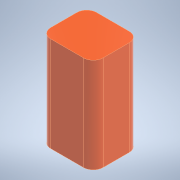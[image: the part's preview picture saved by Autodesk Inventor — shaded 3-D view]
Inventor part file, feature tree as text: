
AUTODESK INVENTOR PART (.ipt)
format: ipt  version: 2022 (Build 260153000, 153)  size: 107,520 bytes
history: native  units: mm
features: other x1, extrude x1, fillet x1, sketch x1
ambient origin geometry x8: Origin, YZ Plane, XZ Plane, XY Plane, X Axis, Y Axis, Z Axis, Center Point
bodies: Body1 (feature_tree)
feature tree (4):
  other  "ソリッド1"
  extrude  "押し出し1"  Depth=32.0mm
  fillet  "フィレット1"  Radius=58.0mm
  sketch  "スケッチ1"
